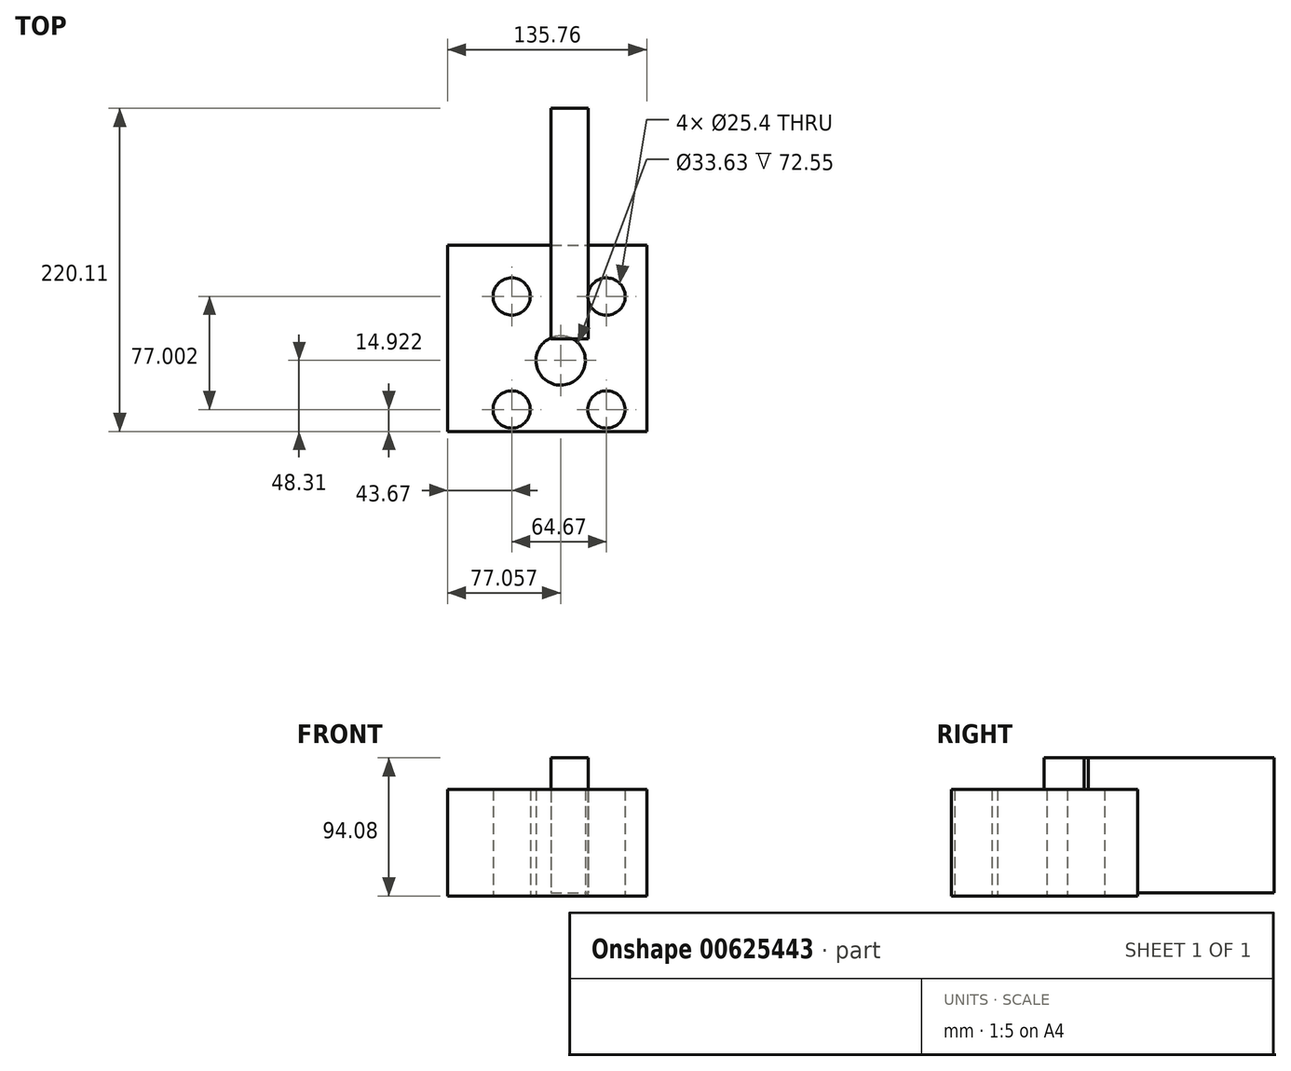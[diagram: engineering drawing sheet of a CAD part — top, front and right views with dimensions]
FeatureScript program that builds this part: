
annotation { "Feature Type Name" : "Feature", "Feature Type Description" : "" }
export const myFeature = defineFeature(function(context is Context, id is Id, definition is map)
    precondition{}
    {
        {
            var Q0;
            Q0=qCreatedBy(makeId("Right.planeOp"),FACE);
            var sketch = newSketch(context, id + "F0", { "sketchPlane" : qUnion([Q0])});
            skLineSegment(sketch, "E0.bottom", {"start": v(-63.87, 50.53) * mm, "end": v(93.11, 50.53) * mm});
            skLineSegment(sketch, "E0.top", {"start": v(-63.87, -41.5) * mm, "end": v(93.11, -41.5) * mm});
            skLineSegment(sketch, "E0.left", {"start": v(-63.87, 50.53) * mm, "end": v(-63.87, -41.5) * mm});
            skLineSegment(sketch, "E0.right", {"start": v(93.11, 50.53) * mm, "end": v(93.11, -41.5) * mm});
            skSolve(sketch);
        }
        {
            var Q0;
            Q0 = qSketchRegion(id + "F0", true);
            extrude(context, id + "F1", {"entities" : qUnion([Q0]), "depth" : 25.4 * mm, "offsetDistance" : 25.4 * mm});
        }
        {
            var Q0;
            Q0=qCreatedBy(makeId("Front.planeOp"),FACE);
            var sketch = newSketch(context, id + "F2", { "sketchPlane" : qUnion([Q0])});
            skLineSegment(sketch, "E1.bottom", {"start": v(-70.32, 29) * mm, "end": v(65.44, 29) * mm});
            skLineSegment(sketch, "E1.top", {"start": v(-70.32, -43.55) * mm, "end": v(65.44, -43.55) * mm});
            skLineSegment(sketch, "E1.left", {"start": v(-70.32, 29) * mm, "end": v(-70.32, -43.55) * mm});
            skLineSegment(sketch, "E1.right", {"start": v(65.44, 29) * mm, "end": v(65.44, -43.55) * mm});
            skSolve(sketch);
        }
        {
            var Q0;
            Q0=makeQuery(id+"F2.imprint","IMPRINT",FACE,{"disambiguationData":[TD([[makeQuery(id+"F2.imprint","IMPRINT",EDGE,{"derivedFrom":sQuery(id+"F2.wireOp",EDGE,"E1.bottom")}),-1.0]])]});
            extrude(context, id + "F3", {"entities" : qUnion([Q0]), "operationType" : NewBodyOperationType.ADD, "endBound" : BoundingType.UP_TO_NEXT, "oppositeDirection" : true, "depth" : 25.4 * mm, "offsetDistance" : 25.4 * mm});
        }
        {
            var Q0;
            Q0=makeQuery(id+"F2.imprint","IMPRINT",FACE,{"disambiguationData":[TD([[makeQuery(id+"F2.imprint","IMPRINT",EDGE,{"derivedFrom":sQuery(id+"F2.wireOp",EDGE,"E1.bottom")}),-1.0]])]});
            extrude(context, id + "F4", {"entities" : qUnion([Q0]), "operationType" : NewBodyOperationType.ADD, "depth" : 127 * mm, "offsetDistance" : 25.4 * mm});
        }
        {
            var Q0;
            Q0=makeQuery(id+"F4.opExtrude","SWEPT_FACE",FACE,{"disambiguationData":[OSD([sQuery(id+"F2.wireOp",EDGE,"E1.top")])]});
            var sketch = newSketch(context, id + "F5", { "sketchPlane" : qUnion([Q0])});
            skLineSegment(sketch, "E2.bottom", {"start": v(38.02, 112.08) * mm, "end": v(-26.65, 112.08) * mm});
            skLineSegment(sketch, "E2.top", {"start": v(38.02, 35.08) * mm, "end": v(-26.65, 35.08) * mm});
            skLineSegment(sketch, "E2.left", {"start": v(38.02, 112.08) * mm, "end": v(38.02, 35.08) * mm});
            skLineSegment(sketch, "E2.right", {"start": v(-26.65, 112.08) * mm, "end": v(-26.65, 35.08) * mm});
            skSolve(sketch);
        }
        {
            var Q0;
            Q0=sQuery(id+"F5.wireOp",VERTEX,"E2.left.start");
            var Q1;
            Q1=sQuery(id+"F5.wireOp",VERTEX,"E2.left.end");
            var Q2;
            Q2=sQuery(id+"F5.wireOp",VERTEX,"E2.right.end");
            var Q3;
            Q3=sQuery(id+"F5.wireOp",VERTEX,"E2.right.start");
            var Q4;
            Q4=makeQuery(id+"F1.opExtrude","SWEPT_BODY",BODY,{"disambiguationData":[OSD([sQuery(id+"F0.wireOp",EDGE,"E0.bottom"),sQuery(id+"F0.wireOp",EDGE,"E0.top"),sQuery(id+"F0.wireOp",EDGE,"E0.left"),sQuery(id+"F0.wireOp",EDGE,"E0.right")])]});
            hole(context, id + "F6", {"style" : HoleStyle.SIMPLE, "endStyle" : HoleEndStyle.THROUGH, "holeDiameter" : 25.4 * mm, "majorDiameter" : 6.35 * mm, "isTappedThrough" : true, "tappedDepth" : 12.7 * mm, "tapClearance" : 3, "locations" : qUnion([Q0, Q1, Q2, Q3]), "scope" : qUnion([Q4])});
        }
        {
            var Q0;
            Q0=makeQuery(id+"F4.opExtrude","SWEPT_FACE",FACE,{"disambiguationData":[OSD([sQuery(id+"F2.wireOp",EDGE,"E1.top")])]});
            var sketch = newSketch(context, id + "F7", { "sketchPlane" : qUnion([Q0])});
            skSolve(sketch);
        }
        {
            var Q0;
            {var subQ0=sQuery(id+"F2.wireOp",EDGE,"E1.top");Q0=makeQuery(id+"F7.imprint","IMPRINT",FACE,{"disambiguationData":[TD([[makeQuery(id+"F7.imprint","IMPRINT",EDGE,{"derivedFrom":makeQuery(id+"F4.opExtrude","CAP_EDGE",EDGE,{"disambiguationData":[OSD([subQ0])],"isStart":true})}),1.0]])]});}
            var sketch = newSketch(context, id + "F8", { "sketchPlane" : qUnion([Q0])});
            skCircle(sketch, "E3", {"center": v(6.74, 78.69) * mm, "radius": 16.81 * mm});
            skSolve(sketch);
        }
        {
            var Q0;
            Q0 = qSketchRegion(id + "F8", true);
            var Q1;
            Q1=makeQuery(id+"F4.opExtrude","SWEPT_FACE",FACE,{"disambiguationData":[OSD([sQuery(id+"F2.wireOp",EDGE,"E1.bottom")])]});
            extrude(context, id + "F9", {"entities" : qUnion([Q0]), "operationType" : NewBodyOperationType.REMOVE, "endBound" : BoundingType.UP_TO_SURFACE, "oppositeDirection" : true, "depth" : 25.4 * mm, "endBoundEntityFace" : qUnion([Q1]), "offsetDistance" : 25.4 * mm});
        }
    });
